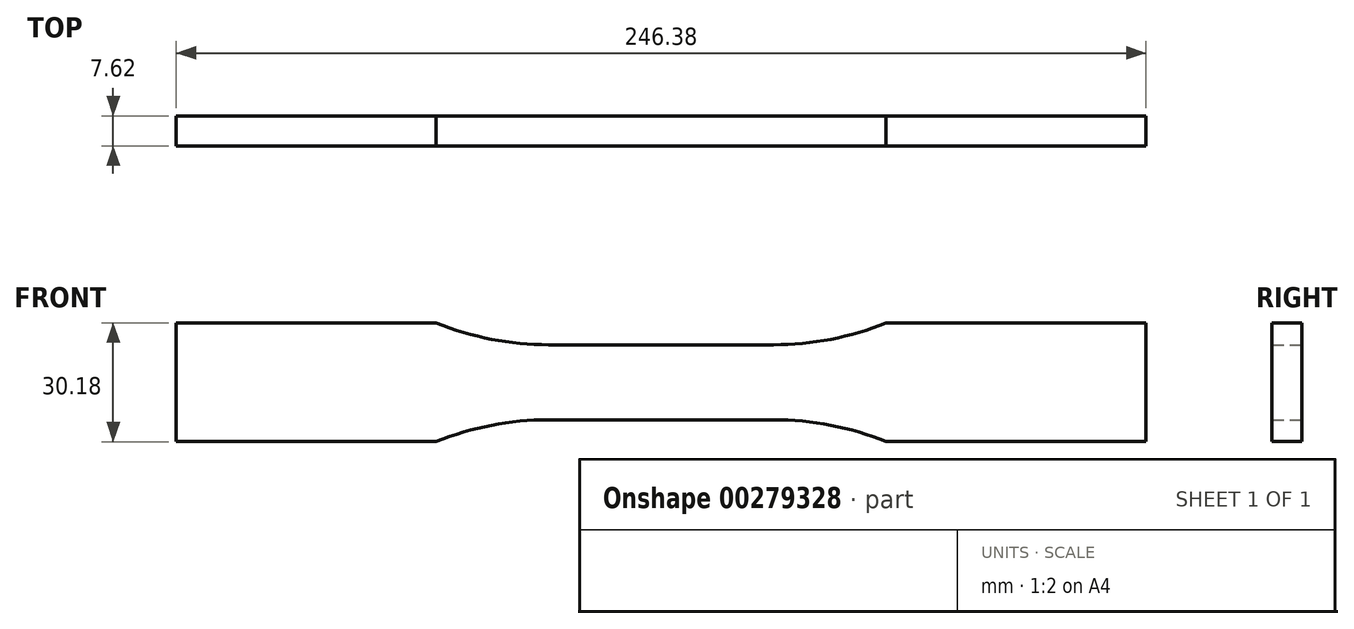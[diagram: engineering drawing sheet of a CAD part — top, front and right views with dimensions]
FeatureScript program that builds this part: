
annotation { "Feature Type Name" : "Feature", "Feature Type Description" : "" }
export const myFeature = defineFeature(function(context is Context, id is Id, definition is map)
    precondition{}
    {
        {
            var Q0;
            Q0=qCreatedBy(makeId("Front.planeOp"),FACE);
            var sketch = newSketch(context, id + "F0", { "sketchPlane" : qUnion([Q0])});
            skLineSegment(sketch, "E0", {"start": v(0, 9.52) * mm, "end": v(28.58, 9.52) * mm});
            skArc(sketch, "E1", {"start": v(28.58, 9.52) * mm, "mid": v(43.13, 10.93) * mm, "end": v(57.15, 15.09) * mm});
            skLineSegment(sketch, "E2", {"start": v(57.15, 15.09) * mm, "end": v(123.2, 15.09) * mm});
            skLineSegment(sketch, "E3.MirrorCS", {"start": v(57.15, -15.09) * mm, "end": v(123.2, -15.09) * mm});
            skLineSegment(sketch, "E4.MirrorCS", {"start": v(0, -9.52) * mm, "end": v(28.58, -9.52) * mm});
            skArc(sketch, "E5.MirrorCS", {"start": v(28.58, -9.52) * mm, "mid": v(43.13, -10.93) * mm, "end": v(57.15, -15.09) * mm});
            skLineSegment(sketch, "E6.MirrorCS", {"start": v(0, 9.53) * mm, "end": v(-28.58, 9.52) * mm});
            skArc(sketch, "E7.MirrorCS", {"start": v(-28.58, 9.52) * mm, "mid": v(-43.13, 10.93) * mm, "end": v(-57.15, 15.09) * mm});
            skLineSegment(sketch, "E8.MirrorCS", {"start": v(-57.15, 15.09) * mm, "end": v(-123.2, 15.09) * mm});
            skLineSegment(sketch, "E9.MirrorCS", {"start": v(-57.15, -15.09) * mm, "end": v(-123.2, -15.09) * mm});
            skArc(sketch, "E10.MirrorCS", {"start": v(-28.58, -9.52) * mm, "mid": v(-43.13, -10.93) * mm, "end": v(-57.15, -15.09) * mm});
            skLineSegment(sketch, "E11.MirrorCS", {"start": v(0, -9.52) * mm, "end": v(-28.58, -9.52) * mm});
            skLineSegment(sketch, "E12", {"start": v(123.2, 15.09) * mm, "end": v(123.2, -15.09) * mm});
            skLineSegment(sketch, "E13", {"start": v(-123.2, 15.09) * mm, "end": v(-123.2, -15.09) * mm});
            skSolve(sketch);
        }
        {
            var Q0;
            Q0=makeQuery(id+"F0.imprint","IMPRINT",FACE,{"disambiguationData":[TD([[makeQuery(id+"F0.imprint","IMPRINT",EDGE,{"derivedFrom":sQuery(id+"F0.wireOp",EDGE,"E1")}),-1.0]])]});
            extrude(context, id + "F1", {"entities" : qUnion([Q0]), "depth" : 7.62 * mm});
        }
    });
